# Revit family: PANZERI_HILOW_SUSPENSION_LIGHT
name_source: partatom
category: Lighting Fixtures
revit_build: Autodesk Revit 2018 (Build: 20190510_1515(x64)
units: mm (PartAtom-declared; Revit-internal decimal feet)

## family parameters
Cut with Voids When Loaded = No
Host = Face
Light Source = Yes
OmniClass Number = 23.80.70.00
OmniClass Title = Lighting
Part Type = Normal
Room Calculation Point = Yes
Round Connector Dimension = Use Diameter
Shared = No

## types (2) — shared parameters
ACCESSORIES = DRIVER: integrated included | Canopy for power supply with 3 outputs and covering included
AVAILABLE FINISHES = Structure and Canopy covering: white, mat black, bronze, mat brass or titanium; Diffusers: Opaline or black screen. CUSTOM finishes available only on request.
Apparent Load = 0 VA
BIM BADGE = https://bim.archiproducts.com
CABLE MATERIAL = PANZERI_PVC_TRANSPARENT
CANOPY MATERIAL = PANZERI_ALUMINIUM_POLYACRYLIC_PAINT_MAT_BRASS_19
COLLECTION = HILOW
COLOR RENDERING INDEX = Ra>90
Color Filter = 16777215
DEPTH = 820 mm
Default Elevation = 1219 mm
Description = Suspension lighting fixture for interiors, with direct and indirect light emission.‎
Dimming Lamp Color Temperature Shift = <None>
ENERGY EFFICIENCY CLASS = N/D
FREQUENCY = 0 Hz
FREQUENCY RANGE = 50/60Hz
HEIGHT = 70 mm
INSTALLATION INSTRUCTIONS = https://panzeri.it
IP RATING = IP20
Lamp = LED
Light Source Symbol Size = 300 mm
MATERIAL DESCRIPTION = Extruded aluminium structure in polyacrylic paint. Joints in turned brass and die-cast aluminium in polyacrylic paint. Die-cast aluminium end caps in polyacrylic paint. Extruded polycarbonate diffusers with opaline or black finish. Reversible suspension kit with griplocks and 5m <196,9in> long steel cables. 5m <196,9in> long power cable in transparent PVC.
Manufacturer = PANZERI
Model = HILOW SUSPENSION
PACKAGING = 87,0 x 118,0 x 14,0 cm
POWER SUPPLY = 220-240V AC
PRODUCT SHEET = https://www.archiproducts.com
STRUCTURE MATERIAL = PANZERI_ALUMINIUM_POLYACRYLIC_PAINT_MAT_BRASS_19
TECHNICAL SHEET = https://panzeri.it
Tilt Angle = -90.00°
Type Comments = Direct and indirect light emission.
URL = https://panzeri.it
USAGE = INDOOR - SUSPENSION
VOLTAGE = 0 V
WATTAGE = 80 W
WEIGHT = 2.80 kg
WIDTH = 1130 mm

## per-type parameters (varying)
| type | LAMP MATERIAL | LIGHTING SPECIFICATION | PRODUCT CODE | Photometric Web File |
| HighEmission_OpalScreen_MatBrass | PANZERI_POLYCARBONATE_OPALINE_SCREEN_Light_on | LED 80W / 2700K / Ra>90 / 5045lm / 220-240V AC / dimmable (DALI /Push DIM) | L02819.115.0502 | Hilow opal suspended L028__.115.0502 - 9072.IES |
| SoftEmission_BlackScreen_MatBrass | PANZERI_POLYCARBONATE_BLACK_SCREEN_Light_on | LED 80W / 2700K / Ra>90 / 2118lm / 220-240V AC / dimmable (DALI /Push DIM) | L02919.115.0502 | Hilow black suspended L029__.115.0502 - 9072.IES |

## geometry (parser evidence)
native form markers: Sweep x7
no freeform markers — native parametric forms only
